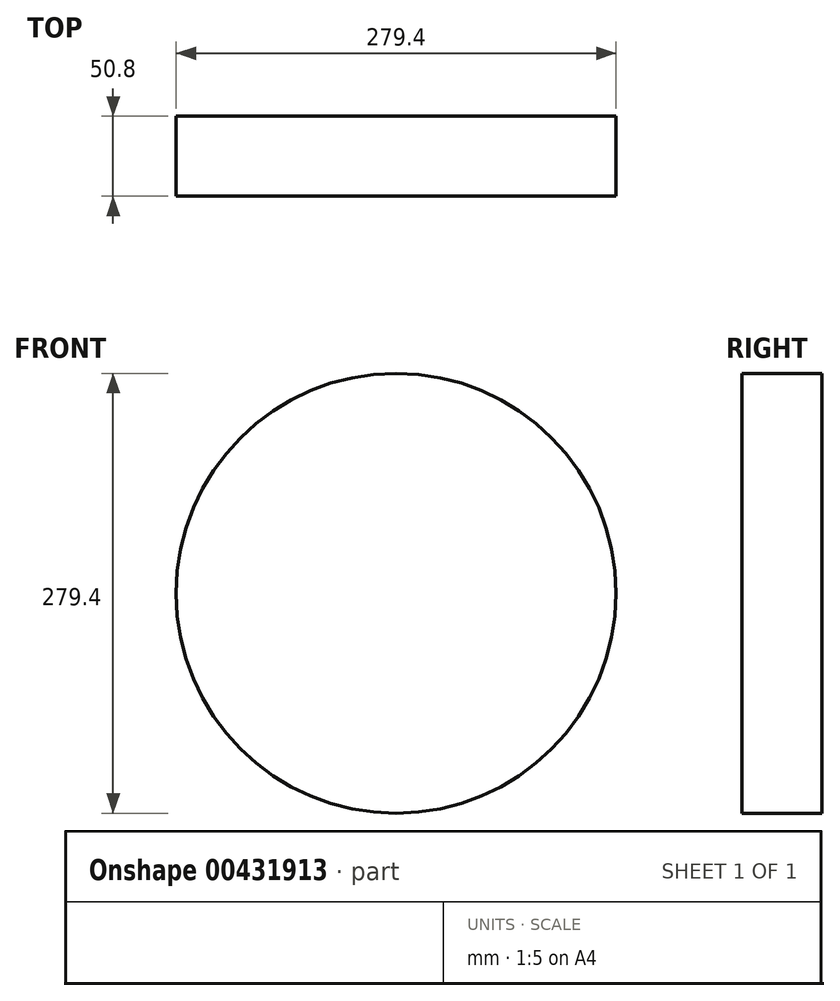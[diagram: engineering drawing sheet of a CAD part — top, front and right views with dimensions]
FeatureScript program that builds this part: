
annotation { "Feature Type Name" : "Feature", "Feature Type Description" : "" }
export const myFeature = defineFeature(function(context is Context, id is Id, definition is map)
    precondition{}
    {
        {
            var Q0;
            Q0=qCreatedBy(makeId("Front.planeOp"),FACE);
            var sketch = newSketch(context, id + "F0", { "sketchPlane" : qUnion([Q0])});
            skCircle(sketch, "E0", {"center": v(0, 0) * mm, "radius": 139.7 * mm});
            skSolve(sketch);
        }
        {
            var Q0;
            Q0 = qSketchRegion(id + "F0", true);
            extrude(context, id + "F1", {"entities" : qUnion([Q0]), "depth" : 50.8 * mm});
        }
    });
